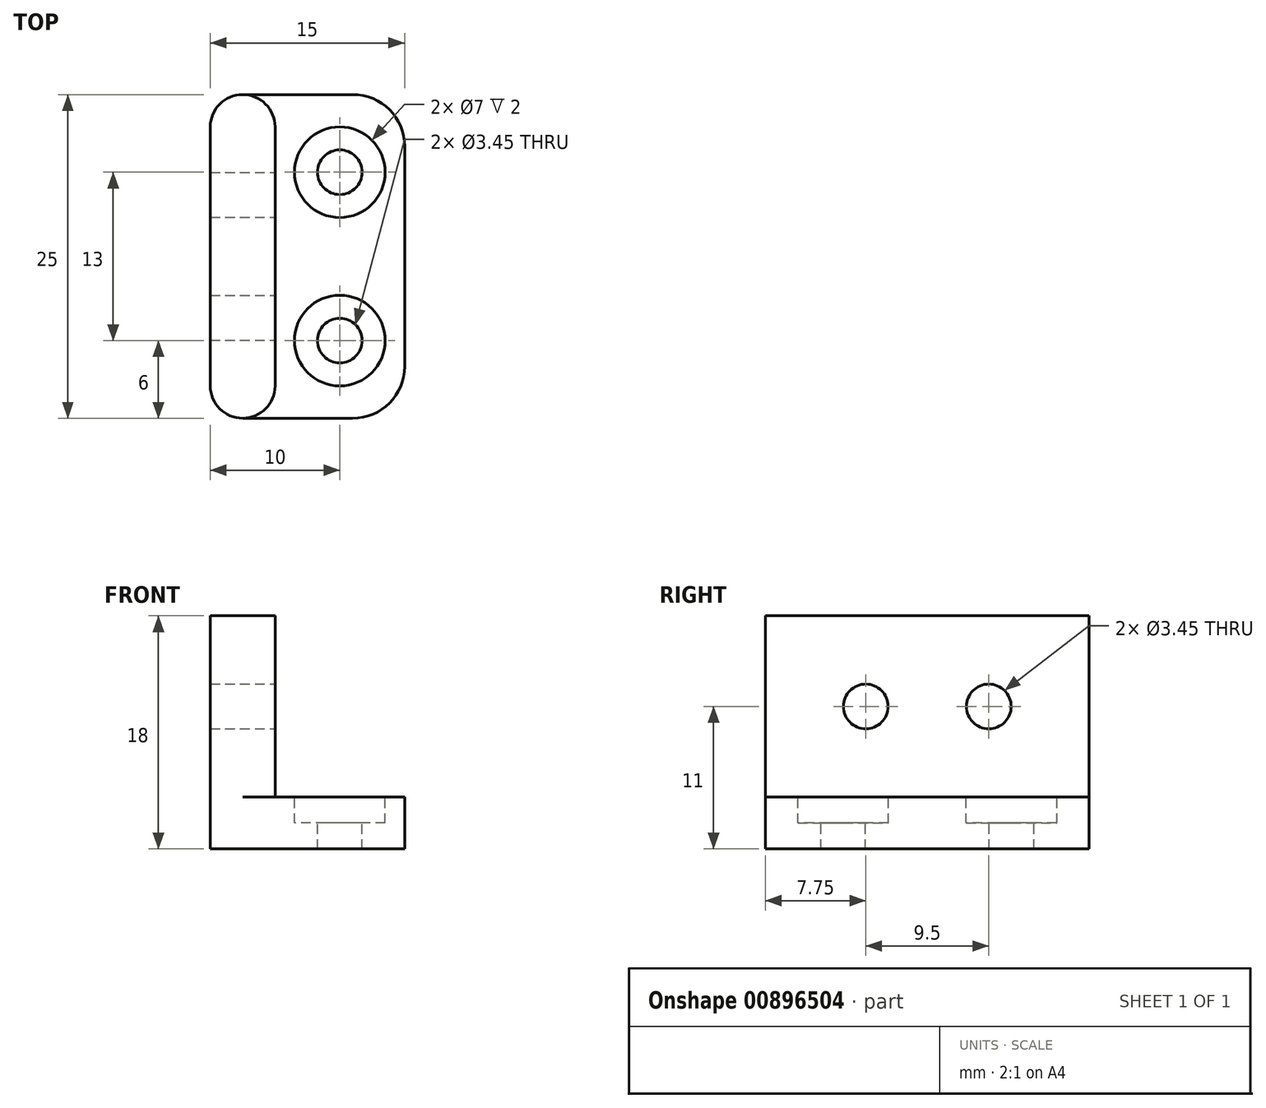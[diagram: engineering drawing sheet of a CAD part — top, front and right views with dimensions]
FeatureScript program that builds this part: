
annotation { "Feature Type Name" : "Feature", "Feature Type Description" : "" }
export const myFeature = defineFeature(function(context is Context, id is Id, definition is map)
    precondition{}
    {
        {
            var Q0;
            Q0=qCreatedBy(makeId("Top.planeOp"),FACE);
            var sketch = newSketch(context, id + "F0", { "sketchPlane" : qUnion([Q0])});
            skLineSegment(sketch, "E0.bottom", {"start": v(0, 0) * mm, "end": v(15, 0) * mm});
            skLineSegment(sketch, "E0.top", {"start": v(0, 25) * mm, "end": v(15, 25) * mm});
            skLineSegment(sketch, "E0.left", {"start": v(0, 0) * mm, "end": v(0, 25) * mm});
            skLineSegment(sketch, "E0.right", {"start": v(15, 0) * mm, "end": v(15, 25) * mm});
            skSolve(sketch);
        }
        {
            var Q0;
            Q0 = qSketchRegion(id + "F0", true);
            extrude(context, id + "F1", {"entities" : qUnion([Q0]), "depth" : 4 * mm, "offsetDistance" : 25 * mm});
        }
        {
            var Q0;
            Q0=makeQuery(id+"F1.opExtrude","CAP_FACE",FACE,{"disambiguationData":[OSD([sQuery(id+"F0.wireOp",EDGE,"E0.bottom"),sQuery(id+"F0.wireOp",EDGE,"E0.top"),sQuery(id+"F0.wireOp",EDGE,"E0.left"),sQuery(id+"F0.wireOp",EDGE,"E0.right")])],"isStart":false});
            var sketch = newSketch(context, id + "F2", { "sketchPlane" : qUnion([Q0])});
            skLineSegment(sketch, "E1.bottom", {"start": v(0, 0) * mm, "end": v(5, 0) * mm});
            skLineSegment(sketch, "E1.top", {"start": v(0, 25) * mm, "end": v(5, 25) * mm});
            skLineSegment(sketch, "E1.left", {"start": v(0, 0) * mm, "end": v(0, 25) * mm});
            skLineSegment(sketch, "E1.right", {"start": v(5, 0) * mm, "end": v(5, 25) * mm});
            skSolve(sketch);
        }
        {
            var Q0;
            Q0 = qSketchRegion(id + "F2", true);
            extrude(context, id + "F3", {"entities" : qUnion([Q0]), "operationType" : NewBodyOperationType.ADD, "depth" : 14 * mm, "offsetDistance" : 25 * mm});
        }
        {
            var Q0;
            Q0=makeQuery(id+"F1.opExtrude","CAP_FACE",FACE,{"disambiguationData":[OSD([sQuery(id+"F0.wireOp",EDGE,"E0.bottom"),sQuery(id+"F0.wireOp",EDGE,"E0.top"),sQuery(id+"F0.wireOp",EDGE,"E0.left"),sQuery(id+"F0.wireOp",EDGE,"E0.right")])],"isStart":false});
            var sketch = newSketch(context, id + "F4", { "sketchPlane" : qUnion([Q0])});
            skLineSegment(sketch, "E2", {"start": v(10, 25) * mm, "end": v(10, 0) * mm, "construction": true});
            skCircle(sketch, "E3", {"center": v(10, 19) * mm, "radius": 3.5 * mm});
            skCircle(sketch, "E4", {"center": v(10, 6) * mm, "radius": 3.5 * mm});
            skCircle(sketch, "E5", {"center": v(10, 19) * mm, "radius": 1.73 * mm});
            skCircle(sketch, "E6", {"center": v(10, 6) * mm, "radius": 1.73 * mm});
            skSolve(sketch);
        }
        {
            var Q0;
            Q0 = qSketchRegion(id + "F4", true);
            extrude(context, id + "F5", {"entities" : qUnion([Q0]), "operationType" : NewBodyOperationType.REMOVE, "oppositeDirection" : true, "depth" : 2 * mm, "offsetDistance" : 25 * mm});
        }
        {
            var Q0;
            Q0=makeQuery(id+"F4.imprint","IMPRINT",FACE,{"disambiguationData":[TD([[makeQuery(id+"F4.imprint","IMPRINT",EDGE,{"derivedFrom":sQuery(id+"F4.wireOp",EDGE,"E5")}),1.0]])]});
            var Q1;
            Q1=makeQuery(id+"F4.imprint","IMPRINT",FACE,{"disambiguationData":[TD([[makeQuery(id+"F4.imprint","IMPRINT",EDGE,{"derivedFrom":sQuery(id+"F4.wireOp",EDGE,"E6")}),1.0]])]});
            extrude(context, id + "F6", {"entities" : qUnion([Q0, Q1]), "operationType" : NewBodyOperationType.REMOVE, "endBound" : BoundingType.UP_TO_NEXT, "oppositeDirection" : true, "depth" : 25 * mm, "offsetDistance" : 25 * mm});
        }
        {
            var Q0;
            Q0=makeQuery(id+"F3.opExtrude","SWEPT_FACE",FACE,{"disambiguationData":[OSD([sQuery(id+"F2.wireOp",EDGE,"E1.right")])]});
            var sketch = newSketch(context, id + "F7", { "sketchPlane" : qUnion([Q0])});
            skCircle(sketch, "E7", {"center": v(7.75, 11) * mm, "radius": 1.73 * mm});
            skCircle(sketch, "E8", {"center": v(17.25, 11) * mm, "radius": 1.73 * mm});
            skLineSegment(sketch, "E9", {"start": v(17.25, 11) * mm, "end": v(7.75, 11) * mm, "construction": true});
            skLineSegment(sketch, "E10", {"start": v(12.5, 18) * mm, "end": v(12.5, 11) * mm, "construction": true});
            skLineSegment(sketch, "E11", {"start": v(25, 11) * mm, "end": v(17.25, 11) * mm, "construction": true});
            skSolve(sketch);
        }
        {
            var Q0;
            Q0 = qSketchRegion(id + "F7", true);
            extrude(context, id + "F8", {"entities" : qUnion([Q0]), "operationType" : NewBodyOperationType.REMOVE, "endBound" : BoundingType.UP_TO_NEXT, "oppositeDirection" : true, "depth" : 25 * mm, "offsetDistance" : 25 * mm});
        }
        {
            var Q0;
            Q0=makeQuery(id+"F1.opExtrude","SWEPT_EDGE",EDGE,{"disambiguationData":[OSD([sQuery(id+"F0.wireOp",EDGE,"E0.bottom"),sQuery(id+"F0.wireOp",EDGE,"E0.right")])]});
            var Q1;
            Q1=makeQuery(id+"F1.opExtrude","SWEPT_EDGE",EDGE,{"disambiguationData":[OSD([sQuery(id+"F0.wireOp",EDGE,"E0.top"),sQuery(id+"F0.wireOp",EDGE,"E0.right")])]});
            fillet(context, id + "F9", {"entities" : qUnion([Q0, Q1]), "tangentPropagation" : true, "radius" : 4 * mm, "defaultsChanged" : false, "vertexSettings" : [], "allowEdgeOverflow" : false});
        }
        {
            var Q0;
            Q0=makeQuery(id+"F3.boolean.opBoolean","MERGE",EDGE,{"derivedFrom":[makeQuery(id+"F1.opExtrude","SWEPT_EDGE",EDGE,{"disambiguationData":[OSD([sQuery(id+"F0.wireOp",EDGE,"E0.bottom"),sQuery(id+"F0.wireOp",EDGE,"E0.left")])]}),makeQuery(id+"F3.opExtrude","SWEPT_EDGE",EDGE,{"disambiguationData":[OSD([sQuery(id+"F2.wireOp",EDGE,"E1.bottom"),sQuery(id+"F2.wireOp",EDGE,"E1.left")])]})]});
            var Q1;
            Q1=makeQuery(id+"F3.boolean.opBoolean","MERGE",EDGE,{"derivedFrom":[makeQuery(id+"F1.opExtrude","SWEPT_EDGE",EDGE,{"disambiguationData":[OSD([sQuery(id+"F0.wireOp",EDGE,"E0.top"),sQuery(id+"F0.wireOp",EDGE,"E0.left")])]}),makeQuery(id+"F3.opExtrude","SWEPT_EDGE",EDGE,{"disambiguationData":[OSD([sQuery(id+"F2.wireOp",EDGE,"E1.top"),sQuery(id+"F2.wireOp",EDGE,"E1.left")])]})]});
            var Q2;
            Q2=makeQuery(id+"F3.opExtrude","SWEPT_EDGE",EDGE,{"disambiguationData":[OSD([sQuery(id+"F0.wireOp",EDGE,"E0.top"),sQuery(id+"F2.wireOp",EDGE,"E1.top"),sQuery(id+"F2.wireOp",EDGE,"E1.right")])]});
            var Q3;
            Q3=makeQuery(id+"F3.opExtrude","SWEPT_EDGE",EDGE,{"disambiguationData":[OSD([sQuery(id+"F0.wireOp",EDGE,"E0.bottom"),sQuery(id+"F2.wireOp",EDGE,"E1.bottom"),sQuery(id+"F2.wireOp",EDGE,"E1.right")])]});
            fillet(context, id + "F10", {"entities" : qUnion([Q0, Q1, Q2, Q3]), "tangentPropagation" : true, "radius" : 2.5 * mm, "defaultsChanged" : false, "vertexSettings" : [], "allowEdgeOverflow" : false});
        }
    });
